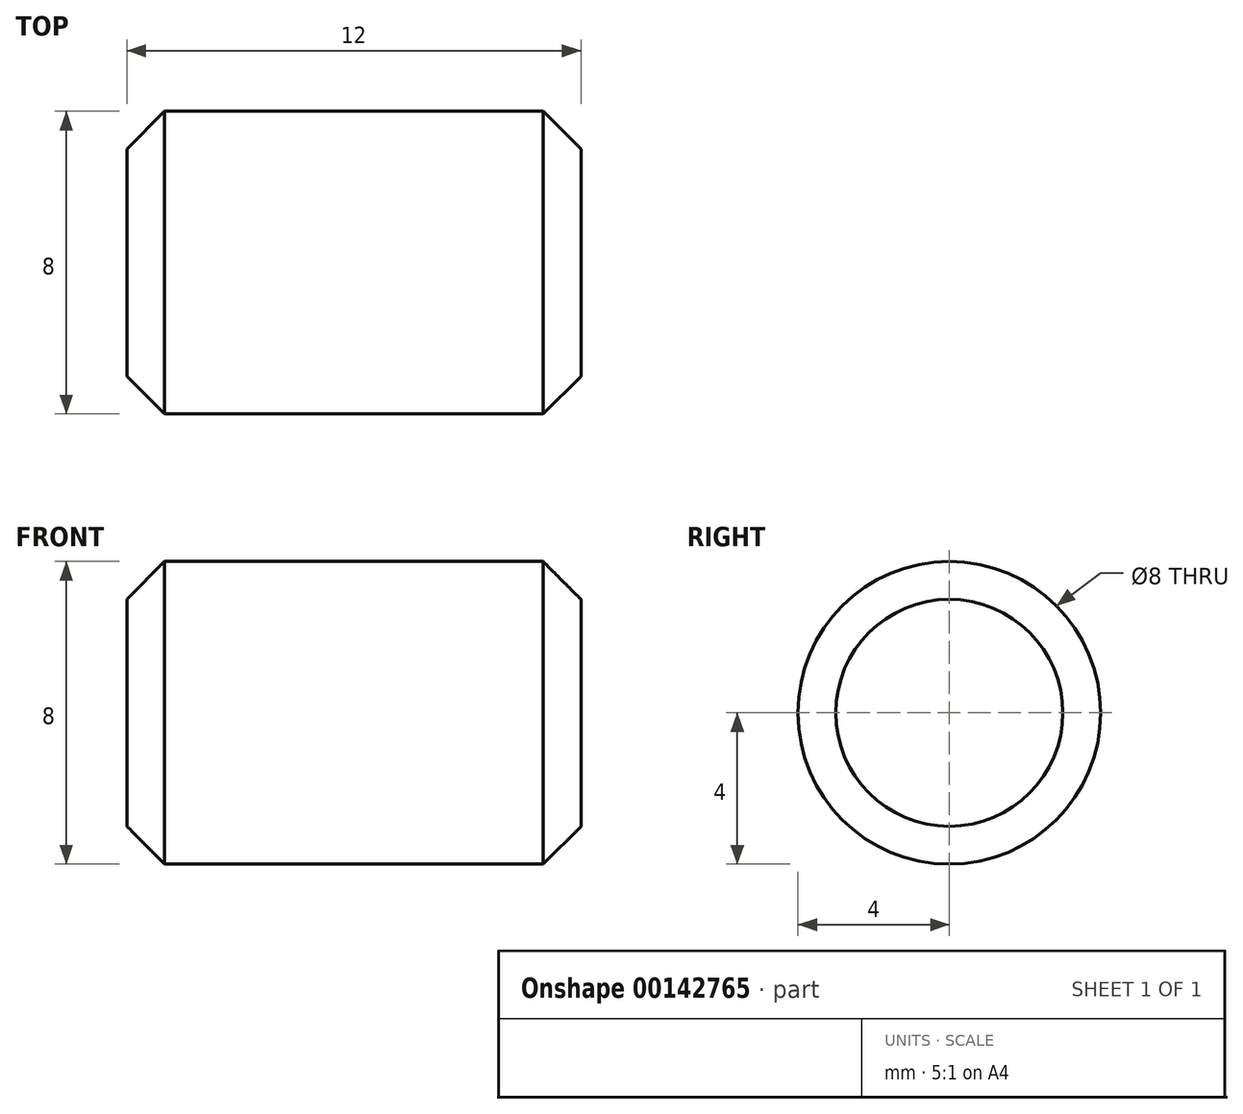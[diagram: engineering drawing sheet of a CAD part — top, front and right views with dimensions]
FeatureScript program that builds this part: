
annotation { "Feature Type Name" : "Feature", "Feature Type Description" : "" }
export const myFeature = defineFeature(function(context is Context, id is Id, definition is map)
    precondition{}
    {
        {
            var Q0;
            Q0=qCreatedBy(makeId("Front.planeOp"),FACE);
            var sketch = newSketch(context, id + "F0", { "sketchPlane" : qUnion([Q0])});
            skLineSegment(sketch, "E0", {"start": v(0, 0) * mm, "end": v(0, 4) * mm});
            skLineSegment(sketch, "E1", {"start": v(12, 4) * mm, "end": v(12, 0) * mm});
            skLineSegment(sketch, "E2", {"start": v(0, 0) * mm, "end": v(17.22, 0) * mm, "construction": true});
            skLineSegment(sketch, "E3", {"start": v(0, 4) * mm, "end": v(12, 4) * mm});
            skSolve(sketch);
        }
        {
            var Q0;
            Q0=sQuery(id+"F0.wireOp",EDGE,"E0");
            var Q1;
            Q1=sQuery(id+"F0.wireOp",EDGE,"E3");
            var Q2;
            Q2=sQuery(id+"F0.wireOp",EDGE,"E1");
            var Q3;
            Q3=sQuery(id+"F0.wireOp",EDGE,"E2");
            revolve(context, id + "F1", {"bodyType" : ToolBodyType.SURFACE, "surfaceEntities" : qUnion([Q0, Q1, Q2]), "axis" : qUnion([Q3]), "revolveType" : RevolveType.FULL});
        }
        {
            var Q0;
            Q0=makeQuery(id+"F1.opRevolve","SWEPT_EDGE",EDGE,{"disambiguationData":[OSD([sQuery(id+"F0.wireOp",VERTEX,"E1.start")])]});
            var Q1;
            Q1=makeQuery(id+"F1.opRevolve","SWEPT_EDGE",EDGE,{"disambiguationData":[OSD([sQuery(id+"F0.wireOp",VERTEX,"E3.start")])]});
            chamfer(context, id + "F2", {"entities" : qUnion([Q0, Q1]), "chamferType" : ChamferType.OFFSET_ANGLE, "width" : 1 * mm, "oppositeDirection" : false, "angle" : 45 * degree, "tangentPropagation" : true});
        }
    });
